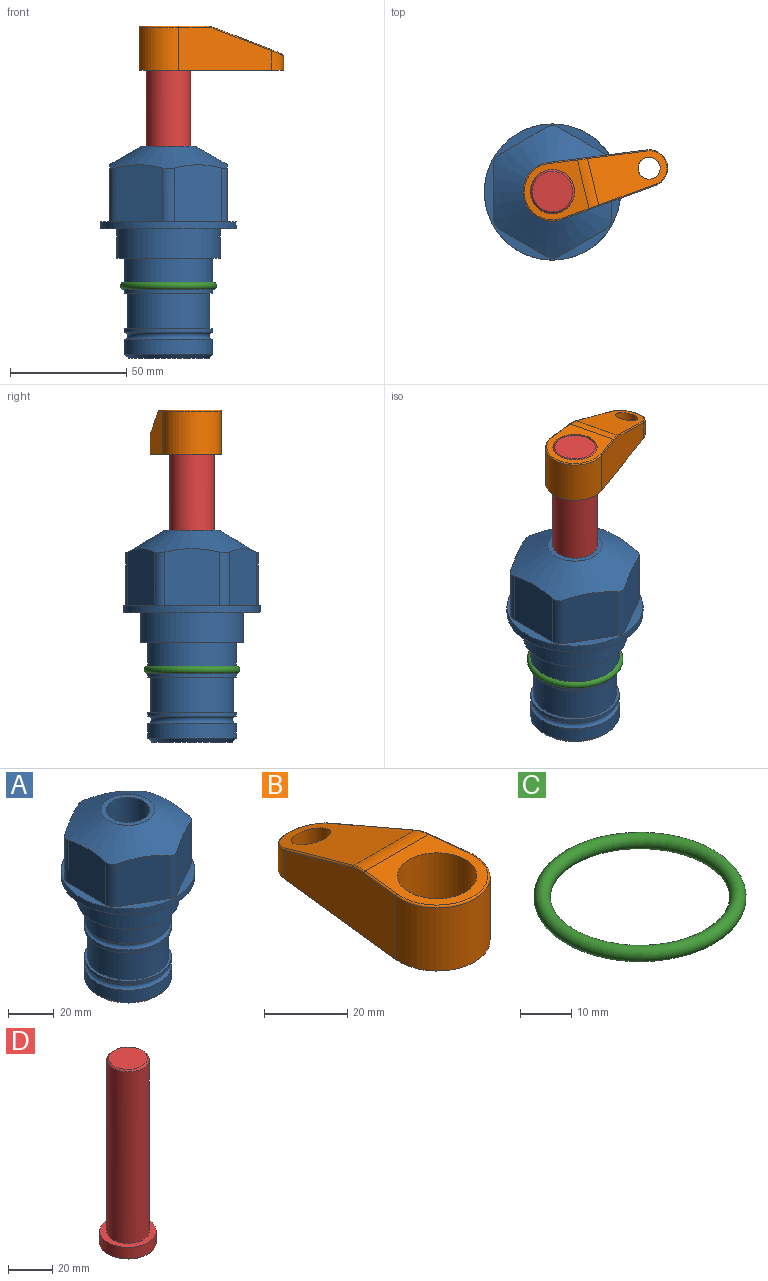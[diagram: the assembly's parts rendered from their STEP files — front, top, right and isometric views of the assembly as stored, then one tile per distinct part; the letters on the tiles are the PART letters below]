
ASSEMBLY  parts=4 mates=2
PART A: 36 faces, bbox 58.7x58.7x91.2 mm
  f0: cylinder r=17.78mm len=35.56mm, axis (0,0,1), area 1670.8mm2, adj f23,f24,f31
  f1: cylinder r=19.05mm len=38.1mm, axis (0,0,1), area 1191.9mm2, adj f26,f27,f30
  f2: plane 58.66x58.66mm, normal (0,0,-1), area 1150.6mm2, adj f3,f28
  f3: cylinder r=29.33mm len=58.66mm, axis (0,0,-1), area 585.1mm2, adj f2,f4
  f4: plane 58.66x58.66mm, normal (0,0,1), area 475.9mm2, adj f3,f5,f6,f7,f8,f9,f10,f11
  f5: plane 24.5x20.32mm, normal (0.5,-0.87,0), area 562.8mm2, adj f4,f15,f16,f17
  f6: plane 24.5x20.32mm, normal (-0.5,-0.87,0), area 562.8mm2, adj f4,f14,f15,f17
  f7: plane 24.5x23.48mm, normal (-1,0,0), area 562.8mm2, adj f4,f13,f14,f17
  f8: plane 24.5x20.32mm, normal (-0.5,0.87,0), area 562.8mm2, adj f4,f12,f13,f17
  f9: plane 24.5x20.32mm, normal (0.5,0.87,0), area 562.8mm2, adj f4,f11,f12,f17
  f10: plane 24.5x23.48mm, normal (1,0,0), area 562.8mm2, adj f4,f11,f16,f17
  f11: cylinder r=5.08mm len=23.01mm, axis (0,0,-1), area 121.2mm2, adj f4,f9,f10,f17
  f12: cylinder r=5.08mm len=23.01mm, axis (0,0,-1), area 121.2mm2, adj f4,f8,f9,f17
  f13: cylinder r=5.08mm len=23.01mm, axis (0,0,-1), area 121.2mm2, adj f4,f7,f8,f17
  f14: cylinder r=5.08mm len=23.01mm, axis (0,0,-1), area 121.2mm2, adj f4,f6,f7,f17
  f15: cylinder r=5.08mm len=23.01mm, axis (0,0,-1), area 121.2mm2, adj f4,f5,f6,f17
  f16: cylinder r=5.08mm len=23.01mm, axis (0,0,-1), area 121.2mm2, adj f4,f5,f10,f17
  f17: cone r=11.73mm half-angle=60deg, axis (0,0,-1), area 2071.8mm2, adj f5,f6,f7,f8,f9,f10,f11,f12
  f18: plane 23.46x23.46mm, normal (0,0,1), area 147.4mm2, adj f17,f35
  f19: plane 34.93x34.93mm, normal (0,0,-1), area 958mm2, adj f29
  f20: cylinder r=19.05mm len=38.1mm, axis (0,0,1), area 760.1mm2, adj f21,f29
  f21: torus R=19.05mm, axis (0,0,1), area 565.3mm2, adj f20,f22
  f22: cylinder r=19.05mm len=38.1mm, axis (0,0,1), area 190mm2, adj f21,f23
  f23: plane 38.1x38.1mm, normal (0,0,1), area 146.9mm2, adj f0,f22
  f24: plane 38.1x38.1mm, normal (0,0,-1), area 146.9mm2, adj f0,f25
  f25: cylinder r=19.05mm len=38.1mm, axis (0,0,1), area 190mm2, adj f24,f26
  f26: torus R=19.05mm, axis (0,0,1), area 565.3mm2, adj f1,f25
  f27: plane 44.45x44.45mm, normal (0,0,-1), area 411.7mm2, adj f1,f28
  f28: cylinder r=22.23mm len=44.45mm, axis (0,0,1), area 1773.5mm2, adj f2,f27
  f29: cone r=19.05mm half-angle=45deg, axis (0,0,1), area 257.5mm2, adj f19,f20
  f30: cylinder r=3.17mm len=6.75mm, axis (-1,0,0), area 128mm2, adj f1,f33
  f31: cylinder r=3.17mm len=6.35mm, axis (-1,0,0), area 102.5mm2, adj f0,f33
  f32: plane 25.4x25.4mm, normal (0,0,1), area 506.7mm2, adj f33
  f33: cylinder r=12.7mm len=66.42mm, axis (0,0,-1), area 5236.2mm2, adj f30,f31,f32,f34
  f34: cone r=9.53mm half-angle=30deg, axis (0,0,-1), area 443.4mm2, adj f33,f35
  f35: cylinder r=9.53mm len=19.05mm, axis (0,0,-1), area 849mm2, adj f18,f34
PART B: 44 faces, bbox 27.5x64.5x19.1 mm
  f0: plane 2.3x0.95mm, normal (0,0,-1), area 1mm2, adj f25,f30,f34
  f1: plane 63.5x25.4mm, normal (0,0,-1), area 561.7mm2, adj f2,f3,f4,f5,f6,f7,f19,f20
  f2: cylinder r=12.7mm len=25.4mm, axis (0,0,-1), area 792.2mm2, adj f1,f3,f5,f13
  f3: plane 42.33x18.54mm, normal (0.99,0.11,0), area 647mm2, adj f1,f2,f4,f11,f12,f14
  f4: cylinder r=7.94mm len=15.78mm, axis (0,0,-1), area 158.6mm2, adj f1,f3,f5,f16
  f5: plane 42.33x18.54mm, normal (-0.99,0.11,0), area 647mm2, adj f1,f2,f4,f15,f17,f18
  f6: cylinder r=9.53mm len=19.05mm, axis (0,0,-1), area 1140.1mm2, adj f1,f8
  f7: cylinder r=4.76mm len=10.98mm, axis (0,0,-1), area 276.1mm2, adj f1,f9
  f8: plane 25.83x24.38mm, normal (0,0,1), area 262.2mm2, adj f6,f10,f11,f13,f15
  f9: plane 32.49x20.55mm, normal (0,0.34,0.94), area 489.9mm2, adj f7,f10,f14,f16,f18
  f10: cylinder r=12.7mm len=21.49mm, axis (-1,0,0), area 93.2mm2, adj f8,f9,f12,f17
  f11: cylinder r=0.51mm len=12.34mm, axis (0.11,-0.99,0), area 9.9mm2, adj f3,f8,f12,f13
  f12: bspline ~7.62x1.64mm, area 3.5mm2, adj f3,f10,f11,f14
  f13: torus R=12.19mm, axis (0,0,1), area 33.6mm2, adj f2,f8,f11,f15
  f14: cylinder r=0.51mm len=26.01mm, axis (0.1,-0.93,0.34), area 21.6mm2, adj f3,f9,f12,f16
  f15: cylinder r=0.51mm len=12.34mm, axis (0.11,0.99,0), area 9.9mm2, adj f5,f8,f13,f17
  f16: bspline ~15.78x7.05mm, area 15.7mm2, adj f4,f9,f14,f18
  f17: bspline ~7.62x1.64mm, area 3.5mm2, adj f5,f10,f15,f18
  f18: cylinder r=0.51mm len=26.01mm, axis (0.1,0.93,-0.34), area 21.6mm2, adj f5,f9,f16,f17
  f19: plane 21.6x14.29mm, normal (-0.99,-0.11,0), area 242.6mm2, adj f1,f26,f28,f34,f36,f38
  f20: plane 21.6x14.29mm, normal (0.99,-0.11,0), area 242.6mm2, adj f1,f27,f29,f37,f39,f41
  f21: cylinder r=12.7mm len=14.29mm, axis (0,0,-1), area 173.2mm2, adj f1,f26,f27,f30,f31,f33
  f22: cylinder r=7.94mm len=7.63mm, axis (0,0,-1), area 53.8mm2, adj f1,f28,f29,f42
  f23: plane 2.3x0.95mm, normal (0,0,-1), area 1mm2, adj f25,f33,f37
  f24: plane 17.94x12.32mm, normal (0,-0.34,-0.94), area 191.2mm2, adj f25,f38,f41,f42
  f25: cylinder r=9.53mm len=12.93mm, axis (-1,0,0), area 37.5mm2, adj f0,f23,f24,f31,f36,f39
  f26: cylinder r=1.59mm len=14.29mm, axis (0,0,-1), area 49mm2, adj f1,f19,f21,f32
  f27: cylinder r=1.59mm len=14.29mm, axis (0,0,-1), area 49mm2, adj f1,f20,f21,f35
  f28: cylinder r=1.59mm len=7.28mm, axis (0,0,-1), area 22.1mm2, adj f1,f19,f22,f40
  f29: cylinder r=1.59mm len=7.28mm, axis (0,0,-1), area 22.1mm2, adj f1,f20,f22,f43
  f30: torus R=14.29mm, axis (0,0,1), area 5.8mm2, adj f0,f21,f31,f32
  f31: bspline ~11.06x2.73mm, area 20.8mm2, adj f21,f25,f30,f33
  f32: sphere r=1.59mm, area 5.4mm2, adj f26,f30,f34
  f33: torus R=14.29mm, axis (0,0,1), area 5.8mm2, adj f21,f23,f31,f35
  f34: cylinder r=1.59mm len=1.68mm, axis (-0.11,0.99,0), area 2.4mm2, adj f0,f19,f32,f36
  f35: sphere r=1.59mm, area 5.4mm2, adj f27,f33,f37
  f36: bspline ~5.82x2.33mm, area 7.7mm2, adj f19,f25,f34,f38
  f37: cylinder r=1.59mm len=1.68mm, axis (0.11,0.99,0), area 2.4mm2, adj f20,f23,f35,f39
  f38: cylinder r=1.59mm len=18.33mm, axis (0.1,-0.93,0.34), area 46.7mm2, adj f19,f24,f36,f40
  f39: bspline ~5.82x2.33mm, area 7.7mm2, adj f20,f25,f37,f41
  f40: sphere r=1.59mm, area 3.6mm2, adj f28,f38,f42
  f41: cylinder r=1.59mm len=18.33mm, axis (0.1,0.93,-0.34), area 46.7mm2, adj f20,f24,f39,f43
  f42: bspline ~8.31x1.84mm, area 15.3mm2, adj f22,f24,f40,f43
  f43: sphere r=1.59mm, area 3.6mm2, adj f29,f41,f42
PART C: 1 faces, bbox 44.7x44.7x3.2 mm
  f0: torus R=19.05mm, axis (0,0,1), area 1193.9mm2
PART D: 6 faces, bbox 25.4x25.4x101.6 mm
  f0: plane 17.46x17.46mm, normal (0,0,1), area 239.5mm2, adj f5
  f1: plane 25.4x25.4mm, normal (0,0,-1), area 506.7mm2, adj f2
  f2: cylinder r=12.7mm len=25.4mm, axis (0,0,1), area 506.7mm2, adj f1,f3
  f3: plane 25.4x25.4mm, normal (0,0,1), area 221.7mm2, adj f2,f4
  f4: cylinder r=9.53mm len=94.46mm, axis (0,0,1), area 5653mm2, adj f3,f5
  f5: cone r=8.73mm half-angle=45deg, axis (0,0,-1), area 64.4mm2, adj f0,f4
PLACE A at identity fixed
PLACE B rot(axis=(0,0,-1),76.3deg) t=(0,0,68.35)mm
PLACE C at identity
PLACE D rot(axis=(0,0,-1),76.3deg) t=(0,0,13.74)mm
MATE fastened B.f2 <-> D.f2  axis (0,0,-1) through (0,0,87.4)mm
MATE cylindrical D.f2 <-> A.f0  axis (0,0,1) through (0,0,39.38)mm
